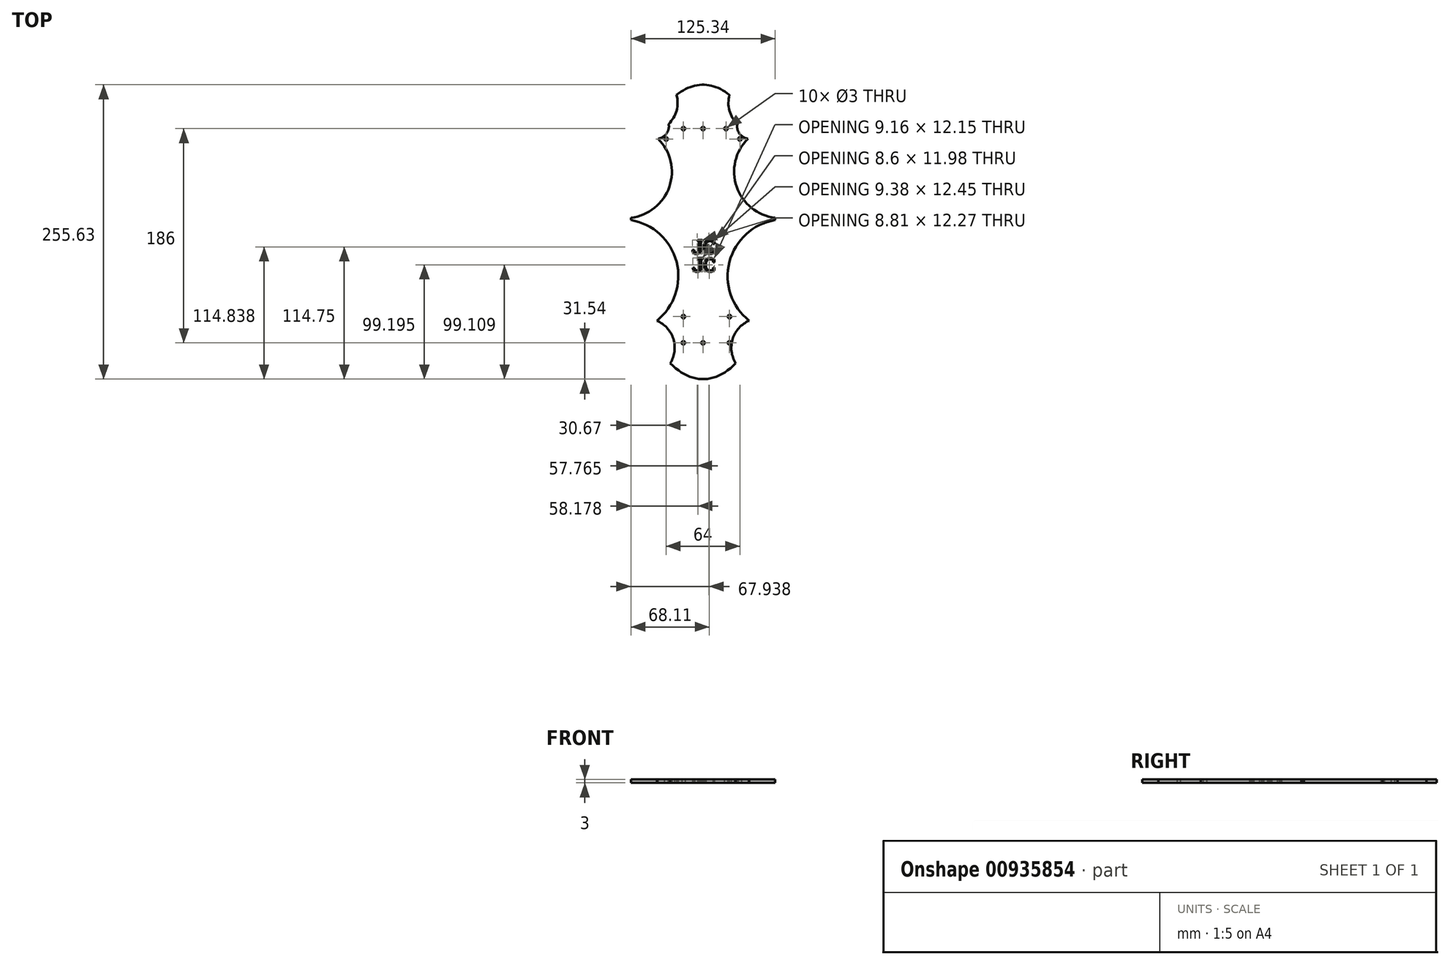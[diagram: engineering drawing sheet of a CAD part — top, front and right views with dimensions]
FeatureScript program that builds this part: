
annotation { "Feature Type Name" : "Feature", "Feature Type Description" : "" }
export const myFeature = defineFeature(function(context is Context, id is Id, definition is map)
    precondition{}
    {
        {
            var Q0;
            Q0=qCreatedBy(makeId("Top.planeOp"),FACE);
            var sketch = newSketch(context, id + "F0", { "sketchPlane" : qUnion([Q0])});
            skCircle(sketch, "E0", {"center": v(-17, -89.5) * mm, "radius": 1.5 * mm});
            skCircle(sketch, "E1", {"center": v(0, -89.5) * mm, "radius": 1.5 * mm});
            skCircle(sketch, "E2", {"center": v(23, -89.5) * mm, "radius": 1.5 * mm});
            skCircle(sketch, "E3", {"center": v(-17, -66.75) * mm, "radius": 1.5 * mm});
            skCircle(sketch, "E4", {"center": v(23, -66.75) * mm, "radius": 1.5 * mm});
            skCircle(sketch, "E5", {"center": v(-17, 96.5) * mm, "radius": 1.5 * mm});
            skCircle(sketch, "E6", {"center": v(0, 96.5) * mm, "radius": 1.5 * mm});
            skCircle(sketch, "E7", {"center": v(20, 96.5) * mm, "radius": 1.5 * mm});
            skCircle(sketch, "E8", {"center": v(32, 87.5) * mm, "radius": 1.5 * mm});
            skCircle(sketch, "E9", {"center": v(-32, 87.5) * mm, "radius": 1.5 * mm});
            skEllipse(sketch, "E10", {"center": v(0, 6.77) * mm, "majorRadius": 127.82 * mm, "minorRadius": 62.88 * mm, "majorAxis": v(0, 1)});
            skText(sketch, "E11", { "text": "JC", "fontName": "RobotoSlab-Regular.ttf"});
            skText(sketch, "E12", { "text": "JC", "fontName": "RobotoSlab-Regular.ttf"});
            skCircle(sketch, "E13", {"center": v(-67.25, 59.1) * mm, "radius": 40.24 * mm});
            skCircle(sketch, "E14", {"center": v(-70.8, -31.62) * mm, "radius": 49.4 * mm});
            skCircle(sketch, "E15.MirrorC", {"center": v(67.25, 59.1) * mm, "radius": 40.24 * mm});
            skCircle(sketch, "E16.MirrorC", {"center": v(70.8, -31.62) * mm, "radius": 49.4 * mm});
            skCircle(sketch, "E17", {"center": v(47.24, 118.77) * mm, "radius": 25.2 * mm});
            skCircle(sketch, "E18.MirrorC", {"center": v(-47.24, 118.77) * mm, "radius": 25.2 * mm});
            skCircle(sketch, "E19", {"center": v(40.43, 98.4) * mm, "radius": 10.8 * mm});
            skCircle(sketch, "E20.MirrorC", {"center": v(-40.43, 98.4) * mm, "radius": 10.8 * mm});
            skCircle(sketch, "E21", {"center": v(50.04, -93.77) * mm, "radius": 25.46 * mm});
            skCircle(sketch, "E22.MirrorC", {"center": v(-50.04, -93.77) * mm, "radius": 25.46 * mm});
            const initialGuessF0  = {"E11": [-0.00984, -0.01225, 1, 0, 0.01225], "E12": [-0.00931, -0.02775, 1, 0, 0.01196]};
            skSetInitialGuess(sketch, initialGuessF0);
            skSolve(sketch);
        }
        {
            var Q0;
            Q0=makeQuery(id+"F0.imprint","IMPRINT",FACE,{"disambiguationData":[TD([[makeQuery(id+"F0.imprint","IMPRINT",EDGE,{"derivedFrom":sQuery(id+"F0.wireOp",EDGE,"E0")}),-1.0]])]});
            extrude(context, id + "F1", {"entities" : qUnion([Q0]), "depth" : 3 * mm, "offsetDistance" : 25 * mm});
        }
    });
